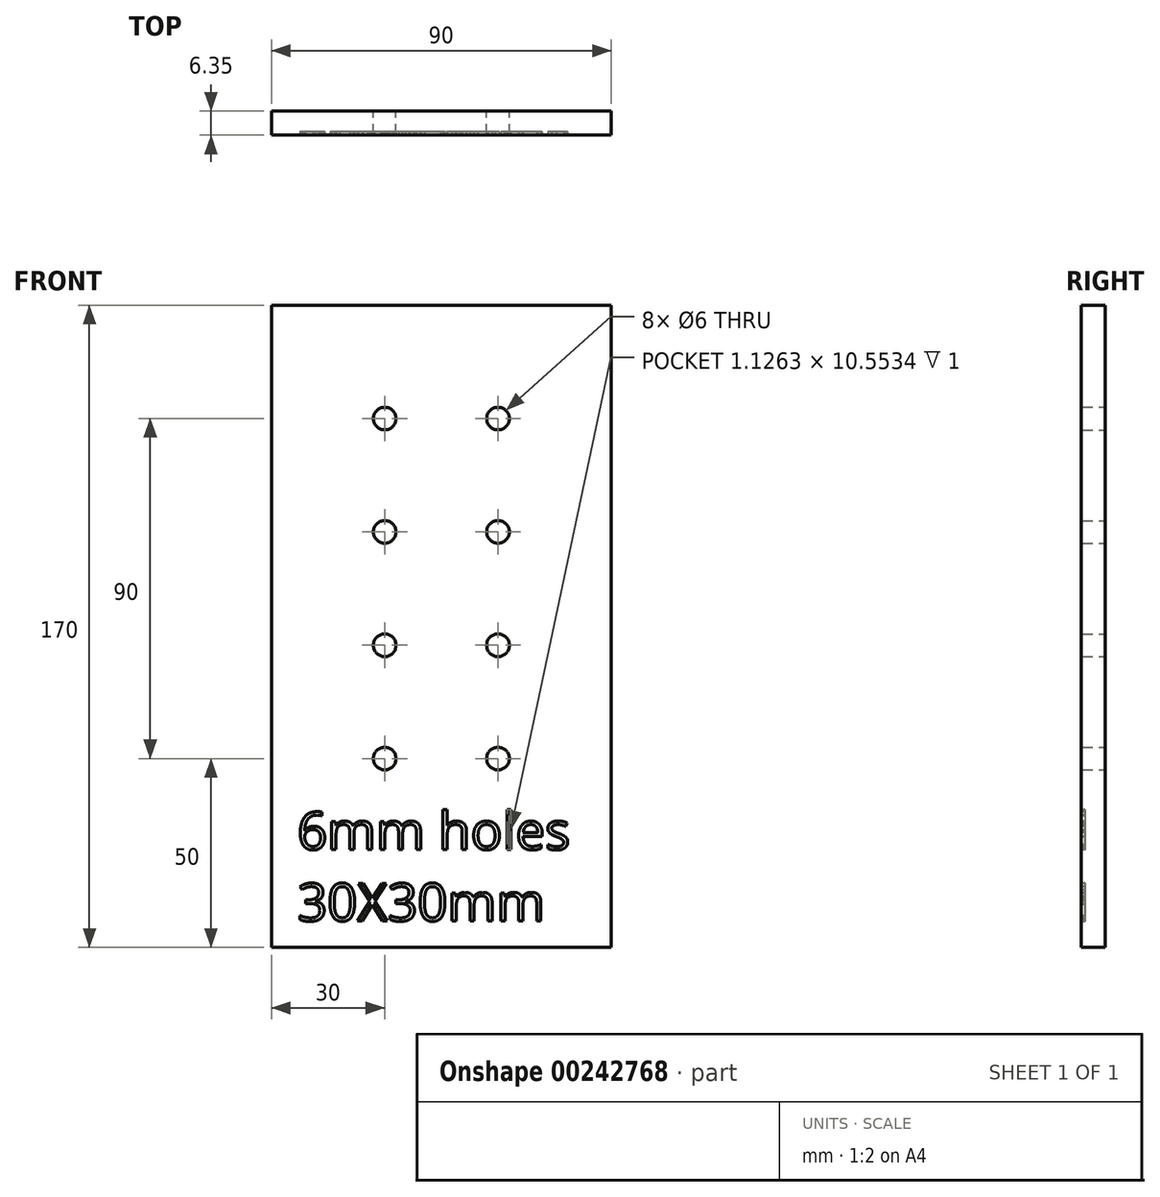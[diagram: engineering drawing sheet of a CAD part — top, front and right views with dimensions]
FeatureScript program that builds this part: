
annotation { "Feature Type Name" : "Feature", "Feature Type Description" : "" }
export const myFeature = defineFeature(function(context is Context, id is Id, definition is map)
    precondition{}
    {
        {
            var Q0;
            Q0=qCreatedBy(makeId("Front.planeOp"),FACE);
            var sketch = newSketch(context, id + "F0", { "sketchPlane" : qUnion([Q0])});
            skLineSegment(sketch, "E0.bottom", {"start": v(-45, 85) * mm, "end": v(45, 85) * mm});
            skLineSegment(sketch, "E0.top", {"start": v(-45, -85) * mm, "end": v(45, -85) * mm});
            skLineSegment(sketch, "E0.left", {"start": v(-45, 85) * mm, "end": v(-45, -85) * mm});
            skLineSegment(sketch, "E1", {"start": v(-15, 85) * mm, "end": v(-15, 55) * mm, "construction": true});
            skLineSegment(sketch, "E2", {"start": v(-15, 55) * mm, "end": v(-45, 55) * mm, "construction": true});
            skCircle(sketch, "E3", {"center": v(-15, 55) * mm, "radius": 3 * mm});
            skLineSegment(sketch, "E4", {"start": v(45, 85) * mm, "end": v(45, -85) * mm});
            skLineSegment(sketch, "E5", {"start": v(-48.1, 0) * mm, "end": v(43.52, 0) * mm, "construction": true});
            skLineSegment(sketch, "E6", {"start": v(0, 55.66) * mm, "end": v(0, -47.1) * mm, "construction": true});
            skCircle(sketch, "E7.0.1.0", {"center": v(-15, 25) * mm, "radius": 3 * mm});
            skCircle(sketch, "E7.1.0.0", {"center": v(15, 55) * mm, "radius": 3 * mm});
            skCircle(sketch, "E7.1.1.0", {"center": v(15, 25) * mm, "radius": 3 * mm});
            skLineSegment(sketch, "E7.direction1", {"start": v(-15, 55) * mm, "end": v(15, 55) * mm, "construction": true});
            skLineSegment(sketch, "E7.direction2", {"start": v(-15, 55) * mm, "end": v(-15, 25) * mm, "construction": true});
            skCircle(sketch, "E8", {"center": v(-415, 250) * mm, "radius": 1.5 * mm});
            skCircle(sketch, "E9.0.0.2", {"center": v(-15, -5) * mm, "radius": 3 * mm});
            skCircle(sketch, "E9.0.0.3", {"center": v(-15, -35) * mm, "radius": 3 * mm});
            skCircle(sketch, "E9.0.1.2", {"center": v(15, -5) * mm, "radius": 3 * mm});
            skCircle(sketch, "E9.0.1.3", {"center": v(15, -35) * mm, "radius": 3 * mm});
            skSolve(sketch);
        }
        {
            var Q0;
            Q0=qSketchRegion(id+"F0",true);
            extrude(context, id + "F1", {"entities" : qUnion([Q0]), "depth" : 6.35 * mm});
        }
        {
            var Q0;
            Q0=makeQuery(id+"F1.opExtrude","SWEPT_BODY",BODY,{"disambiguationData":[OSD([sQuery(id+"F0.wireOp",EDGE,"E8")])]});
            deleteBodies(context, id + "F2", {"entities" : qUnion([Q0])});
        }
        {
            var Q0;
            Q0=makeQuery(id+"F1.opExtrude","CAP_FACE",FACE,{"disambiguationData":[OSD([sQuery(id+"F0.wireOp",EDGE,"E0.bottom"),sQuery(id+"F0.wireOp",EDGE,"E0.top"),sQuery(id+"F0.wireOp",EDGE,"E0.left"),sQuery(id+"F0.wireOp",EDGE,"E3"),sQuery(id+"F0.wireOp",EDGE,"E4"),sQuery(id+"F0.wireOp",EDGE,"E7.0.1.0"),sQuery(id+"F0.wireOp",EDGE,"E7.1.0.0"),sQuery(id+"F0.wireOp",EDGE,"E7.1.1.0"),sQuery(id+"F0.wireOp",EDGE,"E9.0.0.2"),sQuery(id+"F0.wireOp",EDGE,"E9.0.0.3"),sQuery(id+"F0.wireOp",EDGE,"E9.0.1.2"),sQuery(id+"F0.wireOp",EDGE,"E9.0.1.3")])],"isStart":false});
            var sketch = newSketch(context, id + "F3", { "sketchPlane" : qUnion([Q0])});
            skText(sketch, "E10", { "text": "6mm holes\n30X30mm", "fontName": "OpenSans-Regular.ttf"});
            const initialGuessF3  = {"E10": [-0.03814, -0.05909, 1, 0, 0.01]};
            skSetInitialGuess(sketch, initialGuessF3);
            skSolve(sketch);
        }
        {
            var Q0;
            Q0 = qSketchRegion(id + "F3", true);
            extrude(context, id + "F4", {"entities" : qUnion([Q0]), "operationType" : NewBodyOperationType.REMOVE, "oppositeDirection" : true, "depth" : 1 * mm});
        }
    });
